# Revit family: Faucet-Valves_and_Controls-KOHLER-Aqua_Turbo-K-99924IN_1
name_source: partatom
category: Plumbing Fixtures
units: mm (PartAtom-declared; Revit-internal decimal feet)

## family parameters
Cut with Voids When Loaded = No
Host = Face
OmniClass Number = 23.27.31.00
OmniClass Title = Valves
Part Type = Normal
Room Calculation Point = No
Round Connector Dimension = Use Diameter
Shared = No

## types (6) — shared parameters
ADA Compliant = No
Assembly Code = D2020
CW Connection = Yes
Cold Water Inlet = Cold Water Inlet
Date Modified = 08/11/2022
Default Elevation = 50"
Description = High Flow Valve In Polished Chrome
Flow Rate = 15 GPM
HW Connection = Yes
Height = 7 1/8"
Hot Water Inlet = Hot Water Inlet
Length = 4 1/8"
Manufacturer = Kohler Co.
Master Format 2014 = 23 09 13.33
Master Format 2014 Name = Control Valves
Material = Premium Metal Construction
Pressure = 43.51 psi
Product Name = Aqua Turbo
Product Page URL = https://www.kohler.co.in
Tempered Water Outlet 1 = Tempered Water Outlet 1
Tempered Water Outlet 2 = Tempered Water Outlet 2
Tempered Water Outlet 3 = Tempered Water Outlet 3
URL = https://www.kohler.co.in
Vent Connection = No
Waste Connection = No
Waste Water Outlet = Waste Water Outlet
WaterSense Certified = No
Width = 3 13/16"

## per-type parameters (varying)
| type | Finish | Model | Type |
| CP-Polished Chrome | Kohler-Metal-CP-Polished_Chrome | K-99924IN-CP | 1 |
| AF-Vibrant French Gold | Kohler-Metal-AF-Vibrant_French_Gold | K-99924IN-AF | 2 |
| BN-Vibrant Brushed Nickel | Kohler-Metal-BN-Vibrant_Brushed_Nickel | K-99924IN-BN | 3 |
| BL-Matte Black | Kohler-Metal-BL-Matte_Black | K-99924IN-BL | 4 |
| BV-Brushed Bronze | Kohler-Metal-BV-Brushed_Bronze | K-99924IN-BV | 5 |
| RGD-Polished Rose Gold | Kohler-Metal-RGD-Polished_Rose_Gold | K-99924IN-RGD | 6 |

## geometry (parser evidence)
native form markers: Sweep x5
no freeform markers — native parametric forms only
